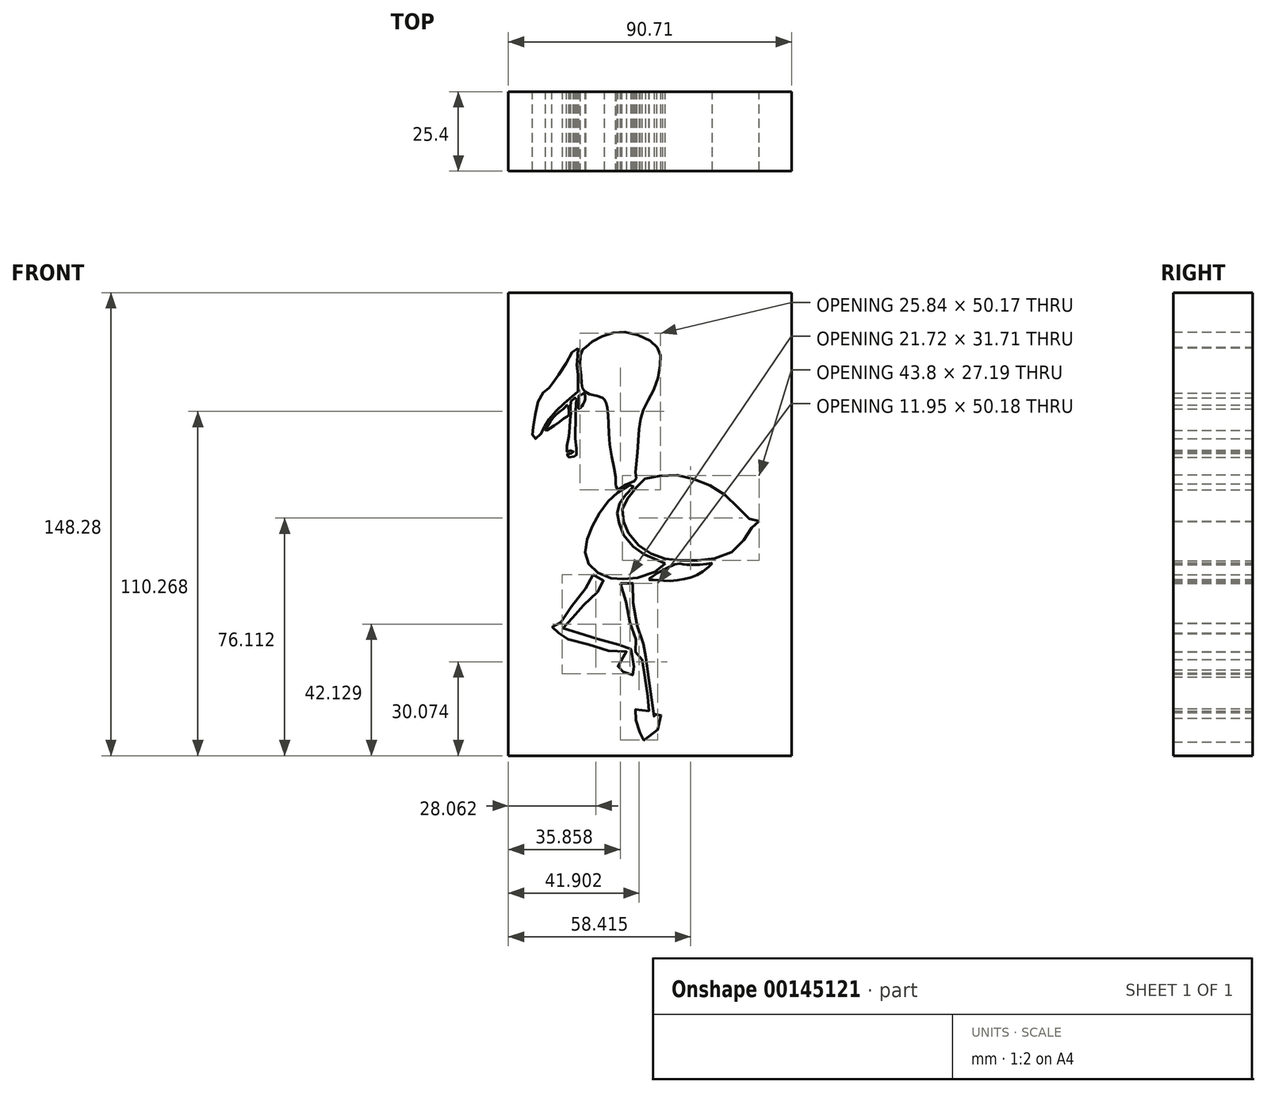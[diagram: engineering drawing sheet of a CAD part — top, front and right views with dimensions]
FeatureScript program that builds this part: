
annotation { "Feature Type Name" : "Feature", "Feature Type Description" : "" }
export const myFeature = defineFeature(function(context is Context, id is Id, definition is map)
    precondition{}
    {
        {
            var Q0;
            Q0=qCreatedBy(makeId("Front.planeOp"),FACE);
            var sketch = newSketch(context, id + "F0", { "sketchPlane" : qUnion([Q0])});
            skFitSpline(sketch, "E0", {"points": [v(-20.2, 55.8) * mm, v(-21.69, 54.43) * mm, v(-21.64, 45.48) * mm, v(-21.18, 42.45) * mm, v(-19.68, 41) * mm, v(-15.04, 39.7) * mm, v(-14.24, 38.96) * mm, v(-13.68, 38.03) * mm, v(-13.1, 34.22) * mm, v(-12.47, 24.13) * mm, v(-10.6, 12.97) * mm, v(-10.67, 11.29) * mm, v(-9.9, 10.1) * mm], "startDerivative": vector(-17.36, -16.45) * mm, "endDerivative": vector(0.06, -29.86) * mm});
            skFitSpline(sketch, "E1", {"points": [v(-20.2, 55.8) * mm, v(-18.03, 57.73) * mm, v(-13.08, 59.92) * mm, v(-8.17, 60.62) * mm, v(-0.96, 58.66) * mm, v(2.5, 55.8) * mm, v(3.7, 53.16) * mm, v(3.46, 48.97) * mm, v(1.79, 42.63) * mm, v(-0.84, 37.85) * mm, v(-2.4, 34.02) * mm, v(-3.11, 30.08) * mm, v(-3.47, 24.81) * mm, v(-3.95, 19.2) * mm, v(-4.31, 15.96) * mm, v(-4.43, 14.53) * mm, v(-3.83, 13.33) * mm, v(-4.2, 13.1) * mm, v(-6.94, 11.96) * mm, v(-9.9, 10.1) * mm], "startDerivative": vector(39.54, 42.31) * mm, "endDerivative": vector(-58.74, -42.9) * mm});
            skFitSpline(sketch, "E2", {"points": [v(-21.23, 40.82) * mm, v(-22.58, 40.14) * mm, v(-22.47, 39.61) * mm, v(-22.58, 36.18) * mm, v(-22.1, 36.18) * mm, v(-20.4, 39.61) * mm, v(-20.89, 41.04) * mm, v(-21.23, 40.82) * mm]});
            skFitSpline(sketch, "E3", {"points": [v(-25.06, 38.37) * mm, v(-23.4, 39.6) * mm, v(-23.07, 39.17) * mm, v(-23.3, 38.27) * mm, v(-23.45, 31.49) * mm, v(-23.69, 27.02) * mm, v(-23.21, 21.3) * mm, v(-23.48, 21.13) * mm, v(-24.55, 20.5) * mm, v(-26.36, 21.08) * mm, v(-25.4, 21.82) * mm, v(-24.33, 21.82) * mm, v(-24.33, 22.62) * mm, v(-25.35, 22.57) * mm, v(-26.3, 22.36) * mm, v(-25.61, 27.1) * mm, v(-25.24, 32.32) * mm, v(-24.97, 35.62) * mm, v(-25.06, 38.37) * mm]});
            skFitSpline(sketch, "E4", {"points": [v(-26.04, 37.17) * mm, v(-25.72, 33.92) * mm, v(-26.04, 33.7) * mm, v(-33.02, 29.12) * mm, v(-31.9, 31.52) * mm, v(-29.5, 34.4) * mm, v(-27, 36.42) * mm, v(-26.04, 37.17) * mm]});
            skFitSpline(sketch, "E5", {"points": [v(-22.67, 55.46) * mm, v(-24.17, 54.68) * mm, v(-27.26, 49.33) * mm, v(-30.58, 44.66) * mm, v(-31.4, 43.53) * mm, v(-32.76, 42.1) * mm, v(-34.65, 40.29) * mm, v(-36.38, 34.33) * mm, v(-37.2, 29.06) * mm, v(-37.28, 27.48) * mm, v(-36.6, 26.5) * mm, v(-35.63, 26.88) * mm, v(-33.82, 29.36) * mm, v(-32.99, 31.25) * mm, v(-30.58, 34.4) * mm, v(-27.26, 37.65) * mm, v(-23.87, 40.66) * mm, v(-22.67, 41.72) * mm, v(-22.67, 42.4) * mm, v(-22.67, 46.39) * mm, v(-23.12, 49.78) * mm, v(-22.74, 53.4) * mm, v(-22.67, 55.46) * mm]});
            skFitSpline(sketch, "E6", {"points": [v(-17.95, -17.1) * mm, v(-16.48, -18.3) * mm, v(-14.33, -19.24) * mm, v(-15.4, -21.4) * mm, v(-18.63, -24.75) * mm, v(-22.67, -28.64) * mm, v(-25.07, -31.6) * mm, v(-27.62, -34.15) * mm, v(-27.08, -34.41) * mm, v(-22.67, -35.76) * mm, v(-17.15, -37.5) * mm, v(-10.03, -39.52) * mm, v(-5.87, -40.32) * mm, v(-5.74, -41.26) * mm, v(-4.93, -45.82) * mm, v(-4.24, -49.85) * mm, v(-6.28, -48.64) * mm, v(-7.89, -48.91) * mm, v(-8.7, -47.57) * mm, v(-9.77, -47.57) * mm, v(-9.77, -46.1) * mm, v(-7.08, -41.93) * mm, v(-10.17, -41.8) * mm, v(-16.75, -40.32) * mm, v(-22.67, -38.58) * mm, v(-27.75, -36.83) * mm, v(-28.56, -35.76) * mm, v(-29.9, -36.02) * mm, v(-31.11, -34.68) * mm, v(-30.04, -32.67) * mm, v(-28.7, -32.67) * mm, v(-26.68, -29.85) * mm, v(-22.67, -24.61) * mm, v(-18.63, -18.57) * mm, v(-17.95, -17.1) * mm]});
            skFitSpline(sketch, "E7", {"points": [v(-9.1, -19.92) * mm, v(-7.08, -19.92) * mm, v(-5.2, -19.78) * mm, v(-5.2, -24.48) * mm, v(-4.26, -29.45) * mm, v(-3.05, -37.5) * mm, v(-1.44, -39.92) * mm, v(-1.05, -42.74) * mm, v(-1.05, -43.8) * mm, v(-0.65, -46.12) * mm, v(1.82, -62.89) * mm, v(2.3, -62.97) * mm, v(2.58, -62.88) * mm, v(2.16, -62.23) * mm, v(1.8, -61.31) * mm, v(2.46, -61.29) * mm, v(3.5, -61.77) * mm, v(4.46, -63.6) * mm, v(2.62, -67.04) * mm, v(0, -69.11) * mm, v(-2.97, -70.55) * mm, v(-2.8, -67.94) * mm, v(-4.24, -66.13) * mm, v(-4.24, -63.68) * mm, v(-5.3, -61.77) * mm, v(-4.24, -60.2) * mm, v(-1.17, -60.43) * mm, v(0, -60.7) * mm, v(0, -59.09) * mm, v(-0.46, -55) * mm, v(-1.13, -50.66) * mm, v(-2.11, -45.24) * mm, v(-2.2, -44.21) * mm, v(-2.83, -44.21) * mm, v(-4.24, -42.06) * mm, v(-4.85, -39.73) * mm, v(-4.24, -37.83) * mm, v(-5.15, -35.17) * mm, v(-6.92, -28.9) * mm, v(-7.89, -23.9) * mm, v(-9.1, -19.92) * mm]});
            skFitSpline(sketch, "E8", {"points": [v(8.32, -13.84) * mm, v(0, -18.59) * mm, v(1.4, -18.78) * mm, v(5.1, -19.06) * mm, v(11.84, -18.4) * mm, v(17.44, -16.03) * mm, v(20.28, -13.37) * mm, v(19.34, -13.56) * mm, v(13.16, -13.94) * mm, v(10.84, -13.7) * mm, v(8.32, -13.84) * mm]});
            skFitSpline(sketch, "E9", {"points": [v(5.24, -13.5) * mm, v(0, -17.07) * mm, v(-7.33, -18.42) * mm, v(-11.8, -18.34) * mm, v(-17.05, -15.97) * mm, v(-19.76, -12.76) * mm, v(-20.35, -8.36) * mm, v(-18.83, -3.28) * mm, v(-16.12, 2.3) * mm, v(-12.49, 7.03) * mm, v(-8.53, 10.18) * mm, v(-4.94, 11.98) * mm, v(-4.79, 11.51) * mm, v(-7, 8.9) * mm, v(-8.9, 6.47) * mm, v(-10.18, 3.6) * mm, v(-9.78, 0.5) * mm, v(-8.9, -2.83) * mm, v(-5.3, -7.75) * mm, v(-0.88, -10.95) * mm, v(3.96, -12.76) * mm, v(5.24, -13.5) * mm]});
            skFitSpline(sketch, "E10", {"points": [v(35.3, 0) * mm, v(34.3, -0.85) * mm, v(32.43, -2.73) * mm, v(30, -6.58) * mm, v(25.7, -10.34) * mm, v(19.52, -12.22) * mm, v(14.15, -12.58) * mm, v(8.06, -12.4) * mm, v(4.38, -11.78) * mm, v(0, -9.98) * mm, v(-3.6, -7.39) * mm, v(-6.64, -3.62) * mm, v(-7.9, -0.85) * mm, v(-8.52, 2.02) * mm, v(-8.34, 4.98) * mm, v(-6.82, 7.4) * mm, v(-4.13, 10.62) * mm, v(-1.98, 13.22) * mm, v(0, 13.94) * mm, v(5.82, 14.83) * mm, v(11.01, 14.48) * mm, v(17.02, 12.6) * mm, v(22.12, 10.09) * mm, v(27.23, 5.79) * mm, v(31, 1.84) * mm, v(33.77, 0) * mm, v(35.3, 0) * mm]});
            skLineSegment(sketch, "E11.bottom", {"start": v(-45.02, 73.2) * mm, "end": v(45.7, 73.2) * mm});
            skLineSegment(sketch, "E11.top", {"start": v(-45.02, -75.08) * mm, "end": v(45.7, -75.08) * mm});
            skLineSegment(sketch, "E11.left", {"start": v(-45.02, 73.2) * mm, "end": v(-45.02, -75.08) * mm});
            skLineSegment(sketch, "E11.right", {"start": v(45.7, 73.2) * mm, "end": v(45.7, -75.08) * mm});
            skSolve(sketch);
        }
        {
            var Q0;
            Q0 = qSketchRegion(id + "F0", true);
            extrude(context, id + "F1", {"entities" : qUnion([Q0]), "depth" : 25.4 * mm});
        }
    });
